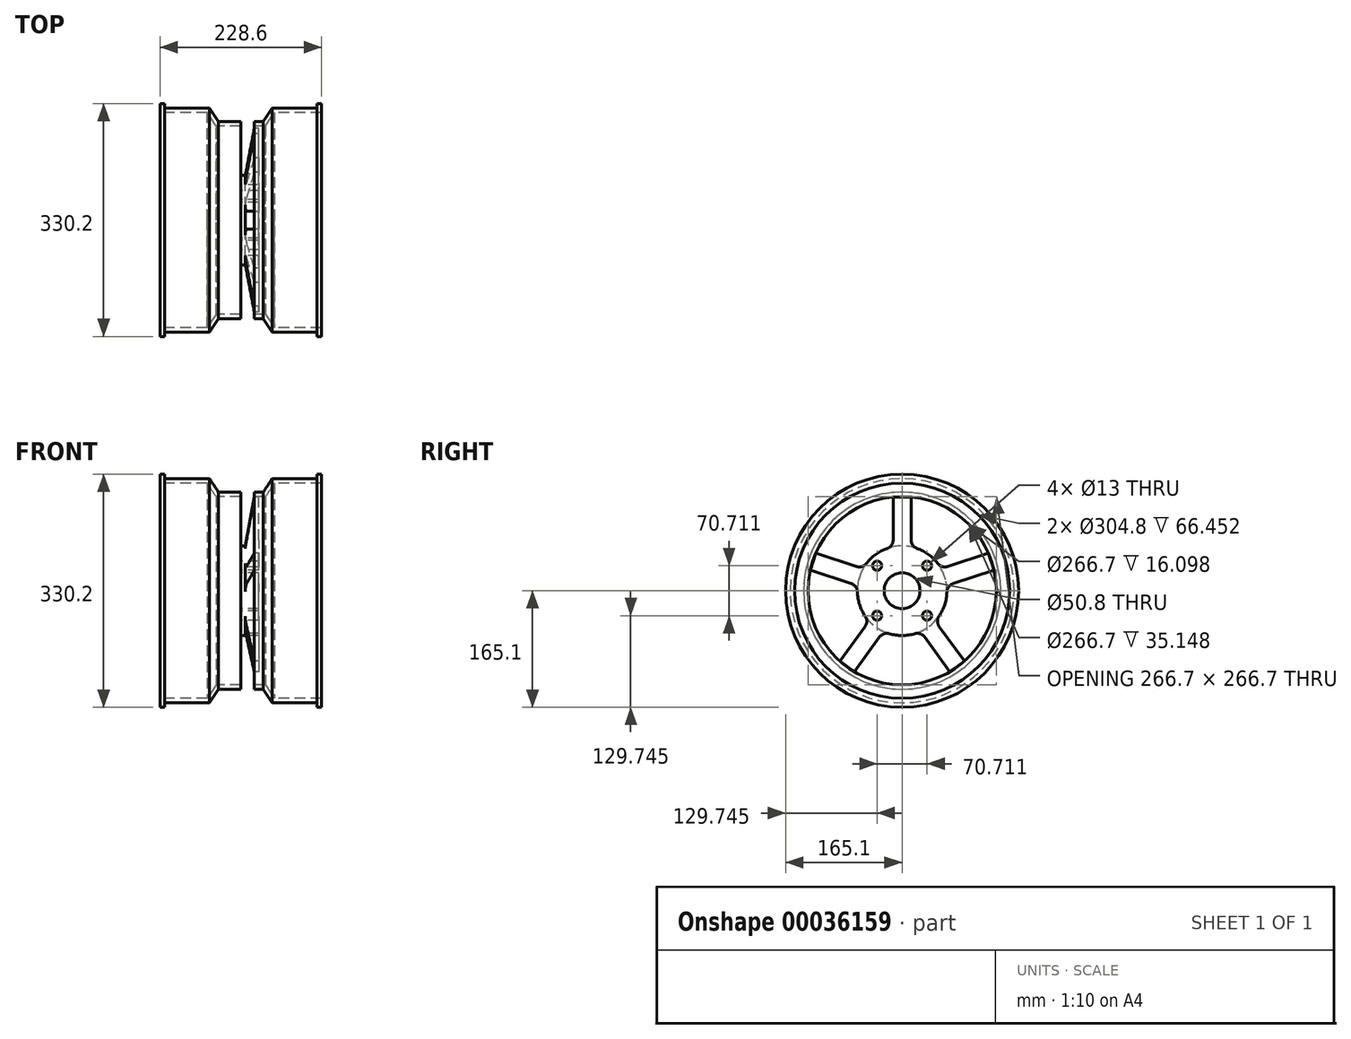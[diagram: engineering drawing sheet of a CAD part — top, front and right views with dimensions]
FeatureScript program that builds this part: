
annotation { "Feature Type Name" : "Feature", "Feature Type Description" : "" }
export const myFeature = defineFeature(function(context is Context, id is Id, definition is map)
    precondition{}
    {
        {
            var Q0;
            Q0=qCreatedBy(makeId("Front.planeOp"),FACE);
            var sketch = newSketch(context, id + "F9", { "sketchPlane" : qUnion([Q0])});
            skLineSegment(sketch, "E0", {"start": v(-114.3, 0) * mm, "end": v(114.3, 0) * mm});
            skLineSegment(sketch, "E1", {"start": v(114.3, 0) * mm, "end": v(114.3, -165.1) * mm});
            skLineSegment(sketch, "E2", {"start": v(114.3, -165.1) * mm, "end": v(107.95, -165.1) * mm});
            skLineSegment(sketch, "E3", {"start": v(107.95, -165.1) * mm, "end": v(107.95, -158.75) * mm});
            skLineSegment(sketch, "E4", {"start": v(107.95, -158.75) * mm, "end": v(44.45, -158.75) * mm});
            skLineSegment(sketch, "E5", {"start": v(31.75, -139.7) * mm, "end": v(-31.75, -139.7) * mm});
            skLineSegment(sketch, "E6", {"start": v(-31.75, -139.7) * mm, "end": v(-44.45, -158.75) * mm});
            skLineSegment(sketch, "E7", {"start": v(-44.45, -158.75) * mm, "end": v(-107.95, -158.75) * mm});
            skLineSegment(sketch, "E8", {"start": v(-107.95, -158.75) * mm, "end": v(-107.95, -165.1) * mm});
            skLineSegment(sketch, "E9", {"start": v(-107.95, -165.1) * mm, "end": v(-114.3, -165.1) * mm});
            skLineSegment(sketch, "E10", {"start": v(-114.3, -165.1) * mm, "end": v(-114.3, 0) * mm});
            skLineSegment(sketch, "E11", {"start": v(31.75, -139.7) * mm, "end": v(44.45, -158.75) * mm});
            skSolve(sketch);
        }
        {
            var Q0;
            Q0=qCreatedBy(makeId("Front.planeOp"),FACE);
            var sketch = newSketch(context, id + "F0", { "sketchPlane" : qUnion([Q0])});
            skLineSegment(sketch, "E12", {"start": v(127, 0) * mm, "end": v(-127, 0) * mm});
            skLineSegment(sketch, "E13", {"start": v(-127, 0) * mm, "end": v(-127, -152.4) * mm});
            skLineSegment(sketch, "E14", {"start": v(-35.15, -133.35) * mm, "end": v(35.15, -133.35) * mm});
            skLineSegment(sketch, "E15", {"start": v(127, -152.4) * mm, "end": v(127, 0) * mm});
            skLineSegment(sketch, "E16", {"start": v(35.15, -133.35) * mm, "end": v(47.85, -152.4) * mm});
            skLineSegment(sketch, "E17", {"start": v(47.85, -152.4) * mm, "end": v(127, -152.4) * mm});
            skLineSegment(sketch, "E18", {"start": v(-35.15, -133.35) * mm, "end": v(-47.85, -152.4) * mm});
            skLineSegment(sketch, "E19", {"start": v(-47.85, -152.4) * mm, "end": v(-127, -152.4) * mm});
            skSolve(sketch);
        }
        {
            var Q0;
            Q0=makeQuery(id+"F9.imprint","IMPRINT",FACE,{"disambiguationData":[TD([[makeQuery(id+"F9.imprint","IMPRINT",EDGE,{"derivedFrom":sQuery(id+"F9.wireOp",EDGE,"E0")}),-1.0]])]});
            var Q1;
            Q1=sQuery(id+"F9.wireOp",EDGE,"E0");
            revolve(context, id + "F1", {"entities" : qUnion([Q0]), "axis" : qUnion([Q1]), "revolveType" : RevolveType.FULL});
        }
        {
            var Q0;
            Q0=makeQuery(id+"F0.imprint","IMPRINT",FACE,{"disambiguationData":[TD([[makeQuery(id+"F0.imprint","IMPRINT",EDGE,{"derivedFrom":sQuery(id+"F0.wireOp",EDGE,"E12")}),1.0]])]});
            var Q1;
            Q1=sQuery(id+"F0.wireOp",EDGE,"E12");
            revolve(context, id + "F2", {"operationType" : NewBodyOperationType.REMOVE, "entities" : qUnion([Q0]), "axis" : qUnion([Q1]), "revolveType" : RevolveType.FULL, "oppositeDirection" : true});
        }
        {
            var Q0;
            Q0=qCreatedBy(makeId("Right.planeOp"),FACE);
            var sketch = newSketch(context, id + "F3", { "sketchPlane" : qUnion([Q0])});
            skLineSegment(sketch, "E20", {"start": v(0, 0) * mm, "end": v(0, 133.35) * mm, "construction": true});
            skLineSegment(sketch, "E21", {"start": v(0, 0) * mm, "end": v(126.82, 41.2) * mm, "construction": true});
            skLineSegment(sketch, "E22", {"start": v(0, 0) * mm, "end": v(78.38, -107.88) * mm, "construction": true});
            skLineSegment(sketch, "E23", {"start": v(0, 0) * mm, "end": v(-78.38, -107.88) * mm, "construction": true});
            skLineSegment(sketch, "E24", {"start": v(0, 0) * mm, "end": v(-126.82, 41.2) * mm, "construction": true});
            skSolve(sketch);
        }
        {
            var Q0;
            Q0=qCreatedBy(makeId("Right.planeOp"),FACE);
            var sketch = newSketch(context, id + "F10", { "sketchPlane" : qUnion([Q0])});
            skCircle(sketch, "E25", {"center": v(0, 0) * mm, "radius": 63.5 * mm});
            skLineSegment(sketch, "E26", {"start": v(12.7, 62.22) * mm, "end": v(12.7, 132.74) * mm});
            skLineSegment(sketch, "E27", {"start": v(-12.7, 62.22) * mm, "end": v(-12.7, 132.74) * mm});
            skCircle(sketch, "E28", {"center": v(0, 0) * mm, "radius": 50 * mm, "construction": true});
            skLineSegment(sketch, "E29", {"start": v(55.25, 31.3) * mm, "end": v(122.32, 53.1) * mm});
            skLineSegment(sketch, "E30", {"start": v(63.1, 7.15) * mm, "end": v(130.17, 28.94) * mm});
            skLineSegment(sketch, "E31", {"start": v(46.84, -42.87) * mm, "end": v(88.3, -99.93) * mm});
            skLineSegment(sketch, "E32", {"start": v(26.3, -57.8) * mm, "end": v(67.75, -114.86) * mm});
            skLineSegment(sketch, "E33", {"start": v(-26.3, -57.8) * mm, "end": v(-67.75, -114.86) * mm});
            skLineSegment(sketch, "E34", {"start": v(-46.84, -42.87) * mm, "end": v(-88.3, -99.93) * mm});
            skLineSegment(sketch, "E35", {"start": v(-63.1, 7.15) * mm, "end": v(-130.17, 28.94) * mm});
            skLineSegment(sketch, "E36", {"start": v(-55.25, 31.3) * mm, "end": v(-122.32, 53.1) * mm});
            skLineSegment(sketch, "E37", {"start": v(-12.7, 132.74) * mm, "end": v(12.7, 132.74) * mm});
            skLineSegment(sketch, "E38", {"start": v(-130.17, 28.94) * mm, "end": v(-122.32, 53.1) * mm});
            skLineSegment(sketch, "E39", {"start": v(122.32, 53.1) * mm, "end": v(130.17, 28.94) * mm});
            skLineSegment(sketch, "E40", {"start": v(88.3, -99.93) * mm, "end": v(67.75, -114.86) * mm});
            skLineSegment(sketch, "E41", {"start": v(-67.75, -114.86) * mm, "end": v(-88.3, -99.93) * mm});
            skSolve(sketch);
        }
        {
            var Q0;
            {var subQ0=sQuery(id+"F10.wireOp",EDGE,"E25");var subQ10=makeQuery(id+"F10.imprint","INTERSECT",VERTEX,{"derivedFrom":[subQ0,sQuery(id+"F10.wireOp",EDGE,"E29")]});Q0=makeQuery(id+"F10.imprint","IMPRINT",FACE,{"disambiguationData":[TD([[makeQuery(id+"F10.imprint","IMPRINT",EDGE,{"disambiguationData":[TD([[subQ10,1.0]])],"derivedFrom":subQ0}),1.0]])]});}
            var Q1;
            {var subQ1=sQuery(id+"F10.wireOp",EDGE,"E26");Q1=makeQuery(id+"F10.imprint","IMPRINT",FACE,{"disambiguationData":[TD([[makeQuery(id+"F10.imprint","IMPRINT",EDGE,{"derivedFrom":subQ1}),1.0]])]});}
            var Q2;
            {var subQ1=sQuery(id+"F10.wireOp",EDGE,"E29");Q2=makeQuery(id+"F10.imprint","IMPRINT",FACE,{"disambiguationData":[TD([[makeQuery(id+"F10.imprint","IMPRINT",EDGE,{"derivedFrom":subQ1}),-1.0]])]});}
            var Q3;
            {var subQ1=sQuery(id+"F10.wireOp",EDGE,"E31");Q3=makeQuery(id+"F10.imprint","IMPRINT",FACE,{"disambiguationData":[TD([[makeQuery(id+"F10.imprint","IMPRINT",EDGE,{"derivedFrom":subQ1}),-1.0]])]});}
            var Q4;
            {var subQ1=sQuery(id+"F10.wireOp",EDGE,"E33");Q4=makeQuery(id+"F10.imprint","IMPRINT",FACE,{"disambiguationData":[TD([[makeQuery(id+"F10.imprint","IMPRINT",EDGE,{"derivedFrom":subQ1}),-1.0]])]});}
            var Q5;
            {var subQ1=sQuery(id+"F10.wireOp",EDGE,"E35");Q5=makeQuery(id+"F10.imprint","IMPRINT",FACE,{"disambiguationData":[TD([[makeQuery(id+"F10.imprint","IMPRINT",EDGE,{"derivedFrom":subQ1}),-1.0]])]});}
            extrude(context, id + "F11", {"entities" : qUnion([Q0, Q1, Q2, Q3, Q4, Q5]), "depth" : 25.4 * mm});
        }
        {
            var Q0;
            Q0=qCreatedBy(makeId("Front.planeOp"),FACE);
            var sketch = newSketch(context, id + "F4", { "sketchPlane" : qUnion([Q0])});
            skLineSegment(sketch, "E42", {"start": v(0, 0) * mm, "end": v(50.8, 0) * mm});
            skLineSegment(sketch, "E43", {"start": v(0, -63.5) * mm, "end": v(0, -165.1) * mm});
            skLineSegment(sketch, "E44", {"start": v(0, -165.1) * mm, "end": v(19.05, -165.1) * mm});
            skLineSegment(sketch, "E45", {"start": v(19.05, -165.1) * mm, "end": v(19.05, -133.35) * mm});
            skLineSegment(sketch, "E46", {"start": v(19.05, -133.35) * mm, "end": v(6.35, -63.5) * mm});
            skLineSegment(sketch, "E47", {"start": v(0, -63.5) * mm, "end": v(6.35, -63.5) * mm});
            skLineSegment(sketch, "E48", {"start": v(1.26, 0) * mm, "end": v(37.05, 0) * mm});
            skLineSegment(sketch, "E49", {"start": v(37.05, 0) * mm, "end": v(37.05, -127) * mm});
            skLineSegment(sketch, "E50", {"start": v(37.05, -127) * mm, "end": v(24.35, -127) * mm});
            skLineSegment(sketch, "E51", {"start": v(24.35, -127) * mm, "end": v(1.26, 0) * mm});
            skSolve(sketch);
        }
        {
            var Q0;
            Q0=makeQuery(id+"F4.imprint","IMPRINT",FACE,{"disambiguationData":[TD([[makeQuery(id+"F4.imprint","IMPRINT",EDGE,{"derivedFrom":sQuery(id+"F4.wireOp",EDGE,"E43")}),1.0]])]});
            var Q1;
            Q1=makeQuery(id+"F4.imprint","IMPRINT",FACE,{"disambiguationData":[TD([[makeQuery(id+"F4.imprint","IMPRINT",EDGE,{"derivedFrom":sQuery(id+"F4.wireOp",EDGE,"E48")}),-1.0]])]});
            var Q2;
            Q2=sQuery(id+"F4.wireOp",EDGE,"E42");
            revolve(context, id + "F5", {"operationType" : NewBodyOperationType.REMOVE, "entities" : qUnion([Q0, Q1]), "axis" : qUnion([Q2]), "revolveType" : RevolveType.FULL, "oppositeDirection" : true});
        }
        {
            var Q0;
            Q0=makeQuery(id+"F11.opExtrude","SWEPT_EDGE",EDGE,{"disambiguationData":[OSD([sQuery(id+"F10.wireOp",EDGE,"E25"),sQuery(id+"F10.wireOp",EDGE,"E26")])]});
            var Q1;
            Q1=makeQuery(id+"F11.opExtrude","SWEPT_EDGE",EDGE,{"disambiguationData":[OSD([sQuery(id+"F10.wireOp",EDGE,"E25"),sQuery(id+"F10.wireOp",EDGE,"E29")])]});
            var Q2;
            Q2=makeQuery(id+"F11.opExtrude","SWEPT_EDGE",EDGE,{"disambiguationData":[OSD([sQuery(id+"F10.wireOp",EDGE,"E25"),sQuery(id+"F10.wireOp",EDGE,"E30")])]});
            var Q3;
            Q3=makeQuery(id+"F11.opExtrude","SWEPT_EDGE",EDGE,{"disambiguationData":[OSD([sQuery(id+"F10.wireOp",EDGE,"E25"),sQuery(id+"F10.wireOp",EDGE,"E31")])]});
            var Q4;
            Q4=makeQuery(id+"F11.opExtrude","SWEPT_EDGE",EDGE,{"disambiguationData":[OSD([sQuery(id+"F10.wireOp",EDGE,"E25"),sQuery(id+"F10.wireOp",EDGE,"E32")])]});
            var Q5;
            Q5=makeQuery(id+"F11.opExtrude","SWEPT_EDGE",EDGE,{"disambiguationData":[OSD([sQuery(id+"F10.wireOp",EDGE,"E25"),sQuery(id+"F10.wireOp",EDGE,"E33")])]});
            var Q6;
            Q6=makeQuery(id+"F11.opExtrude","SWEPT_EDGE",EDGE,{"disambiguationData":[OSD([sQuery(id+"F10.wireOp",EDGE,"E25"),sQuery(id+"F10.wireOp",EDGE,"E34")])]});
            var Q7;
            Q7=makeQuery(id+"F11.opExtrude","SWEPT_EDGE",EDGE,{"disambiguationData":[OSD([sQuery(id+"F10.wireOp",EDGE,"E25"),sQuery(id+"F10.wireOp",EDGE,"E35")])]});
            var Q8;
            Q8=makeQuery(id+"F11.opExtrude","SWEPT_EDGE",EDGE,{"disambiguationData":[OSD([sQuery(id+"F10.wireOp",EDGE,"E25"),sQuery(id+"F10.wireOp",EDGE,"E36")])]});
            var Q9;
            Q9=makeQuery(id+"F11.opExtrude","SWEPT_EDGE",EDGE,{"disambiguationData":[OSD([sQuery(id+"F10.wireOp",EDGE,"E25"),sQuery(id+"F10.wireOp",EDGE,"E27")])]});
            fillet(context, id + "F6", {"entities" : qUnion([Q0, Q1, Q2, Q3, Q4, Q5, Q6, Q7, Q8, Q9]), "radius" : 12.7 * mm, "tangentPropagation" : true, "allowEdgeOverflow" : false});
        }
        {
            var Q0;
            Q0=qCreatedBy(makeId("Right.planeOp"),FACE);
            var sketch = newSketch(context, id + "F12", { "sketchPlane" : qUnion([Q0])});
            skCircle(sketch, "E52", {"center": v(0, 0) * mm, "radius": 50 * mm});
            skLineSegment(sketch, "E53", {"start": v(0, 0) * mm, "end": v(-35.36, 35.36) * mm});
            skLineSegment(sketch, "E54", {"start": v(-35.36, 35.36) * mm, "end": v(0, 0) * mm});
            skLineSegment(sketch, "E55", {"start": v(35.36, 35.36) * mm, "end": v(0, 0) * mm});
            skLineSegment(sketch, "E56", {"start": v(0, 0) * mm, "end": v(35.36, -35.36) * mm});
            skLineSegment(sketch, "E57", {"start": v(0, 0) * mm, "end": v(-35.36, -35.36) * mm});
            skLineSegment(sketch, "E58", {"start": v(0, 0) * mm, "end": v(0, 100.98) * mm, "construction": true});
            skSolve(sketch);
        }
        {
            var Q0;
            Q0=sQuery(id+"F12.wireOp",VERTEX,"E57.end");
            var Q1;
            Q1=sQuery(id+"F12.wireOp",VERTEX,"E54.start");
            var Q2;
            Q2=sQuery(id+"F12.wireOp",VERTEX,"E55.start");
            var Q3;
            Q3=sQuery(id+"F12.wireOp",VERTEX,"E56.end");
            var Q4;
            Q4=makeQuery(id+"F11.opExtrude","SWEPT_BODY",BODY,{"disambiguationData":[OSD([sQuery(id+"F10.wireOp",EDGE,"E25"),sQuery(id+"F10.wireOp",EDGE,"E26"),sQuery(id+"F10.wireOp",EDGE,"E27"),sQuery(id+"F10.wireOp",EDGE,"E29"),sQuery(id+"F10.wireOp",EDGE,"E30"),sQuery(id+"F10.wireOp",EDGE,"E31"),sQuery(id+"F10.wireOp",EDGE,"E32"),sQuery(id+"F10.wireOp",EDGE,"E33"),sQuery(id+"F10.wireOp",EDGE,"E34"),sQuery(id+"F10.wireOp",EDGE,"E35"),sQuery(id+"F10.wireOp",EDGE,"E36"),sQuery(id+"F10.wireOp",EDGE,"E37"),sQuery(id+"F10.wireOp",EDGE,"E38"),sQuery(id+"F10.wireOp",EDGE,"E39"),sQuery(id+"F10.wireOp",EDGE,"E40"),sQuery(id+"F10.wireOp",EDGE,"E41")])]});
            hole(context, id + "F7", {"style" : HoleStyle.SIMPLE, "holeDiameter" : 13 * mm, "endStyle" : HoleEndStyle.THROUGH, "oppositeDirection" : true, "locations" : qUnion([Q0, Q1, Q2, Q3]), "scope" : qUnion([Q4])});
        }
        {
            var Q0;
            Q0=qCreatedBy(makeId("Right.planeOp"),FACE);
            var sketch = newSketch(context, id + "F13", { "sketchPlane" : qUnion([Q0])});
            skCircle(sketch, "E59", {"center": v(0, 0) * mm, "radius": 25.4 * mm});
            skSolve(sketch);
        }
        {
            var Q0;
            Q0=makeQuery(id+"F13.imprint","IMPRINT",FACE,{"disambiguationData":[TD([[makeQuery(id+"F13.imprint","IMPRINT",EDGE,{"derivedFrom":sQuery(id+"F13.wireOp",EDGE,"E59")}),1.0]])]});
            extrude(context, id + "F8", {"entities" : qUnion([Q0]), "operationType" : NewBodyOperationType.REMOVE, "depth" : 25.4 * mm});
        }
    });
